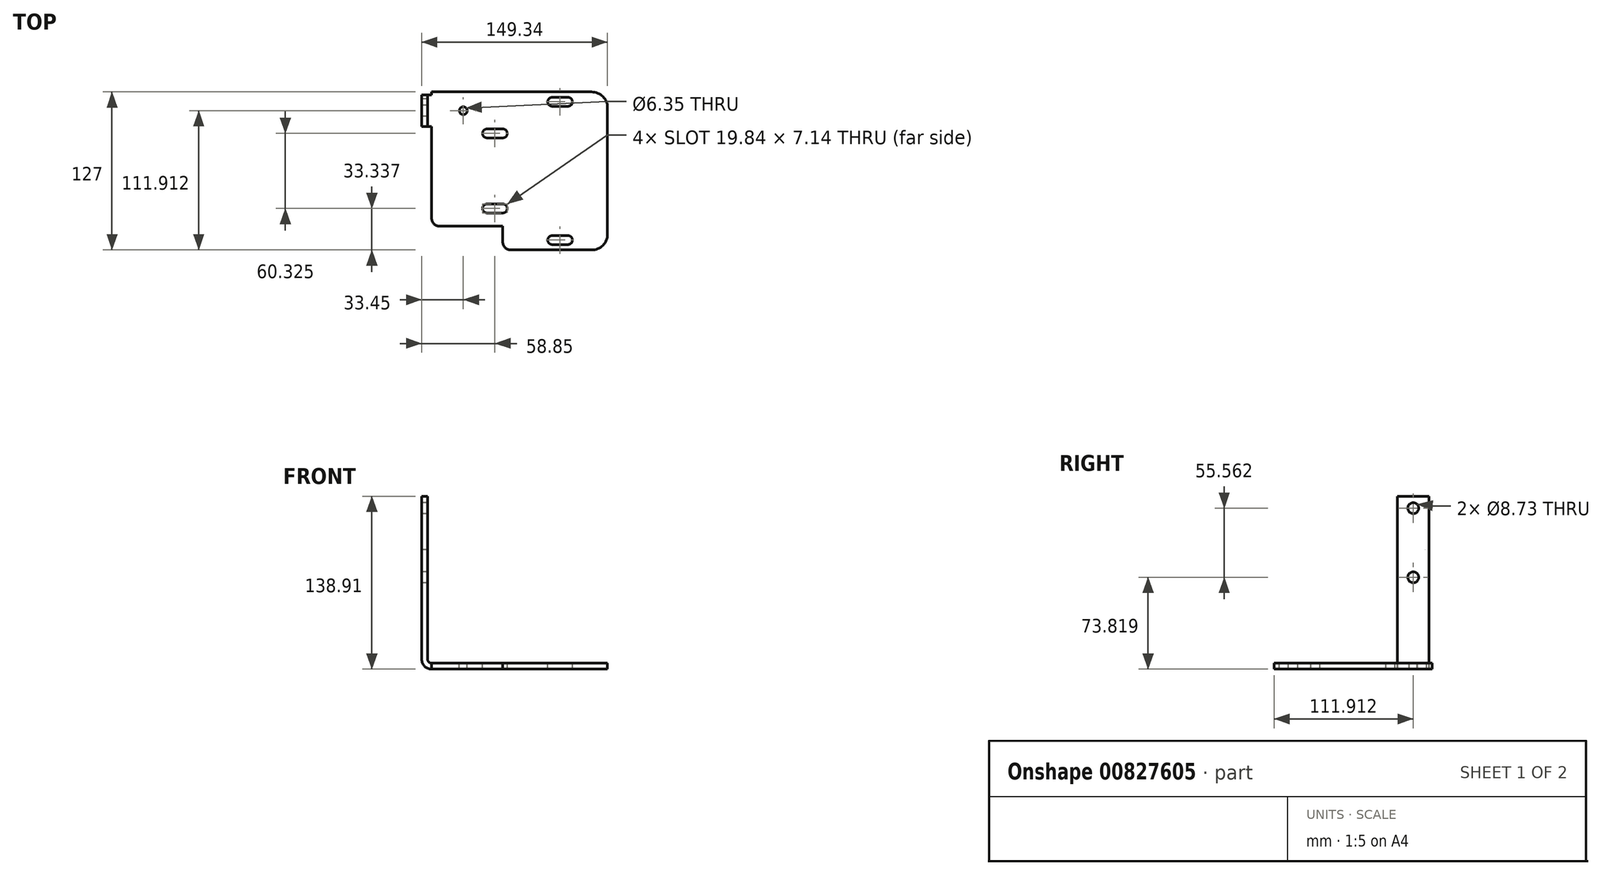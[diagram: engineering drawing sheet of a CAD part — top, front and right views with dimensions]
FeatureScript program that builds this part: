
annotation { "Feature Type Name" : "Feature", "Feature Type Description" : "" }
export const myFeature = defineFeature(function(context is Context, id is Id, definition is map)
    precondition{}
    {
        {
            var Q0;
            Q0=qCreatedBy(makeId("Front.planeOp"),FACE);
            var sketch = newSketch(context, id + "F0", { "sketchPlane" : qUnion([Q0])});
            skLineSegment(sketch, "E0", {"start": v(0, 0) * mm, "end": v(141.29, 0) * mm});
            skArc(sketch, "E1", {"start": v(-8.05, 8.05) * mm, "mid": v(-5.7, 2.36) * mm, "end": v(0, 0) * mm});
            skArc(sketch, "E2.0", {"start": v(-3.29, 8.05) * mm, "mid": v(-2.33, 5.73) * mm, "end": v(0, 4.76) * mm});
            skLineSegment(sketch, "E3", {"start": v(-8.05, 8.05) * mm, "end": v(-8.05, 138.9) * mm});
            skLineSegment(sketch, "E4", {"start": v(-8.05, 138.9) * mm, "end": v(-3.29, 138.9) * mm});
            skLineSegment(sketch, "E5", {"start": v(-3.29, 138.9) * mm, "end": v(-3.29, 8.05) * mm});
            skLineSegment(sketch, "E6", {"start": v(0, 4.76) * mm, "end": v(141.29, 4.76) * mm});
            skLineSegment(sketch, "E7", {"start": v(141.29, 0) * mm, "end": v(141.29, 4.76) * mm});
            skSolve(sketch);
        }
        {
            var Q0;
            Q0 = qSketchRegion(id + "F0", true);
            extrude(context, id + "F1", {"entities" : qUnion([Q0]), "oppositeDirection" : true, "depth" : 127 * mm, "offsetDistance" : 25.4 * mm});
        }
        {
            var Q0;
            Q0=makeQuery(id+"F1.opExtrude","SWEPT_FACE",FACE,{"disambiguationData":[OSD([sQuery(id+"F0.wireOp",EDGE,"E4")])]});
            var sketch = newSketch(context, id + "F2", { "sketchPlane" : qUnion([Q0])});
            skLineSegment(sketch, "E8.bottom", {"start": v(-8.05, 127) * mm, "end": v(0, 127) * mm});
            skLineSegment(sketch, "E8.top", {"start": v(-8.05, 124.61) * mm, "end": v(0, 124.61) * mm});
            skLineSegment(sketch, "E8.left", {"start": v(-8.05, 127) * mm, "end": v(-8.05, 124.61) * mm});
            skLineSegment(sketch, "E8.right", {"start": v(0, 127) * mm, "end": v(0, 124.61) * mm});
            skLineSegment(sketch, "E9.bottom", {"start": v(-8.05, 99.21) * mm, "end": v(0, 99.21) * mm});
            skLineSegment(sketch, "E9.top", {"start": v(-8.05, 0) * mm, "end": v(0, 0) * mm});
            skLineSegment(sketch, "E9.left", {"start": v(-8.05, 99.21) * mm, "end": v(-8.05, 0) * mm});
            skLineSegment(sketch, "E9.right", {"start": v(0, 99.21) * mm, "end": v(0, 0) * mm});
            skSolve(sketch);
        }
        {
            var Q0;
            Q0 = qSketchRegion(id + "F2", true);
            extrude(context, id + "F3", {"entities" : qUnion([Q0]), "operationType" : NewBodyOperationType.REMOVE, "endBound" : BoundingType.THROUGH_ALL, "oppositeDirection" : true, "depth" : 25.4 * mm, "offsetDistance" : 25.4 * mm});
        }
        {
            var Q0;
            Q0=makeQuery(id+"F1.opExtrude","SWEPT_FACE",FACE,{"disambiguationData":[OSD([sQuery(id+"F0.wireOp",EDGE,"E6")])]});
            var sketch = newSketch(context, id + "F4", { "sketchPlane" : qUnion([Q0])});
            skLineSegment(sketch, "E10.0", {"start": v(0, 127) * mm, "end": v(128.59, 127) * mm});
            skLineSegment(sketch, "E10.1", {"start": v(63.5, 0) * mm, "end": v(128.59, 0) * mm});
            skLineSegment(sketch, "E10.2", {"start": v(141.29, 114.3) * mm, "end": v(141.29, 12.7) * mm});
            skLineSegment(sketch, "E10.3", {"start": v(0, 25.4) * mm, "end": v(0, 99.21) * mm});
            skLineSegment(sketch, "E11", {"start": v(6.35, 19.05) * mm, "end": v(57.15, 19.05) * mm});
            skLineSegment(sketch, "E12", {"start": v(57.15, 19.05) * mm, "end": v(57.15, 6.35) * mm});
            skPoint(sketch, "E13.newPointA", {"position": v(57.15, 0) * mm});
            skPoint(sketch, "E13.newPointB", {"position": v(0, 0) * mm});
            skArc(sketch, "E13.filletArc", {"start": v(57.15, 6.35) * mm, "mid": v(59, 1.86) * mm, "end": v(63.5, 0) * mm});
            skPoint(sketch, "E14.newPointB", {"position": v(0, 19.05) * mm});
            skArc(sketch, "E14.filletArc", {"start": v(0, 25.4) * mm, "mid": v(1.86, 20.9) * mm, "end": v(6.35, 19.05) * mm});
            skPoint(sketch, "E15.visualSharp", {"position": v(141.29, 0) * mm});
            skPoint(sketch, "E16.visualSharp", {"position": v(141.29, 127) * mm});
            skArc(sketch, "E16.filletArc", {"start": v(141.29, 114.3) * mm, "mid": v(137.57, 123.28) * mm, "end": v(128.59, 127) * mm});
            skLineSegment(sketch, "E17", {"start": v(0, 99.21) * mm, "end": v(0, 127) * mm});
            skLineSegment(sketch, "E18", {"start": v(128.59, 127) * mm, "end": v(141.29, 127) * mm});
            skLineSegment(sketch, "E19", {"start": v(141.29, 127) * mm, "end": v(141.29, 114.3) * mm});
            skLineSegment(sketch, "E20", {"start": v(0, 0) * mm, "end": v(63.5, 0) * mm});
            skLineSegment(sketch, "E21", {"start": v(0, 0) * mm, "end": v(0, 25.4) * mm});
            skArc(sketch, "E22", {"start": v(57.15, 90.1) * mm, "mid": v(60.72, 93.66) * mm, "end": v(57.15, 97.23) * mm});
            skArc(sketch, "E23", {"start": v(44.45, 97.23) * mm, "mid": v(40.88, 93.66) * mm, "end": v(44.45, 90.1) * mm});
            skLineSegment(sketch, "E24", {"start": v(44.45, 97.23) * mm, "end": v(57.15, 97.23) * mm});
            skPoint(sketch, "E25", {"position": v(141.29, 63.5) * mm});
            skLineSegment(sketch, "E26", {"start": v(57.15, 90.1) * mm, "end": v(44.45, 90.1) * mm});
            skArc(sketch, "E27", {"start": v(57.03, 29.77) * mm, "mid": v(60.72, 33.28) * mm, "end": v(57.15, 36.9) * mm});
            skArc(sketch, "E28", {"start": v(44.45, 36.9) * mm, "mid": v(40.88, 33.34) * mm, "end": v(44.45, 29.77) * mm});
            skLineSegment(sketch, "E29", {"start": v(44.45, 36.9) * mm, "end": v(57.15, 36.9) * mm});
            skLineSegment(sketch, "E30", {"start": v(57.27, 29.77) * mm, "end": v(44.45, 29.77) * mm});
            skArc(sketch, "E31", {"start": v(109.52, 115.5) * mm, "mid": v(113.1, 119.06) * mm, "end": v(109.52, 122.63) * mm});
            skArc(sketch, "E32", {"start": v(96.82, 122.63) * mm, "mid": v(93.25, 119.05) * mm, "end": v(96.84, 115.5) * mm});
            skLineSegment(sketch, "E33", {"start": v(96.82, 122.63) * mm, "end": v(109.52, 122.63) * mm});
            skLineSegment(sketch, "E34.0", {"start": v(-8.05, 124.61) * mm, "end": v(-8.05, 99.21) * mm});
            skLineSegment(sketch, "E35", {"start": v(-8.05, 111.91) * mm, "end": v(25.4, 111.91) * mm});
            skCircle(sketch, "E36", {"center": v(25.4, 111.91) * mm, "radius": 3.18 * mm});
            skArc(sketch, "E37.filletArc", {"start": v(128.59, 0) * mm, "mid": v(137.57, 3.72) * mm, "end": v(141.29, 12.7) * mm});
            skArc(sketch, "E38", {"start": v(109.52, 4.37) * mm, "mid": v(113.1, 7.94) * mm, "end": v(109.52, 11.5) * mm});
            skArc(sketch, "E39", {"start": v(96.82, 11.5) * mm, "mid": v(93.25, 7.93) * mm, "end": v(96.84, 4.37) * mm});
            skLineSegment(sketch, "E40", {"start": v(96.82, 11.5) * mm, "end": v(109.52, 11.5) * mm});
            skLineSegment(sketch, "E41", {"start": v(109.52, 4.37) * mm, "end": v(96.84, 4.37) * mm});
            skLineSegment(sketch, "E42", {"start": v(109.52, 115.5) * mm, "end": v(96.84, 115.5) * mm});
            skSolve(sketch);
        }
        {
            var Q0;
            Q0=makeQuery(id+"F4.imprint","IMPRINT",FACE,{"disambiguationData":[TD([[makeQuery(id+"F4.imprint","IMPRINT",EDGE,{"derivedFrom":sQuery(id+"F4.wireOp",EDGE,"E22")}),1.0]])]});
            var Q1;
            {var subQ5=sQuery(id+"F4.wireOp",EDGE,"E32");Q1=makeQuery(id+"F4.imprint","IMPRINT",FACE,{"disambiguationData":[TD([[makeQuery(id+"F4.imprint","IMPRINT",EDGE,{"derivedFrom":subQ5}),1.0]])]});}
            var Q2;
            {var subQ5=sQuery(id+"F4.wireOp",EDGE,"E28");Q2=makeQuery(id+"F4.imprint","IMPRINT",FACE,{"disambiguationData":[TD([[makeQuery(id+"F4.imprint","IMPRINT",EDGE,{"derivedFrom":subQ5}),1.0]])]});}
            var Q3;
            Q3=makeQuery(id+"F4.imprint","IMPRINT",FACE,{"disambiguationData":[TD([[makeQuery(id+"F4.imprint","IMPRINT",EDGE,{"derivedFrom":sQuery(id+"F4.wireOp",EDGE,"4bc9b2f9-e6e9-4a17-9026-1413efbbbff0")}),1.0]])]});
            var Q4;
            Q4=makeQuery(id+"F4.imprint","IMPRINT",FACE,{"disambiguationData":[TD([[makeQuery(id+"F4.imprint","IMPRINT",EDGE,{"derivedFrom":sQuery(id+"F4.wireOp",EDGE,"E16.filletArc")}),-1.0]])]});
            var Q5;
            Q5=makeQuery(id+"F4.imprint","IMPRINT",FACE,{"disambiguationData":[TD([[makeQuery(id+"F4.imprint","IMPRINT",EDGE,{"derivedFrom":sQuery(id+"F4.wireOp",EDGE,"E15.filletArc")}),-1.0]])]});
            var Q6;
            Q6=makeQuery(id+"F4.imprint","IMPRINT",FACE,{"disambiguationData":[TD([[makeQuery(id+"F4.imprint","IMPRINT",EDGE,{"derivedFrom":sQuery(id+"F4.wireOp",EDGE,"E11")}),-1.0]])]});
            var Q7;
            Q7=makeQuery(id+"F4.imprint","IMPRINT",FACE,{"disambiguationData":[TD([[makeQuery(id+"F4.imprint","IMPRINT",EDGE,{"derivedFrom":sQuery(id+"F4.wireOp",EDGE,"E36")}),1.0]])]});
            var Q8;
            Q8=makeQuery(id+"F4.imprint","IMPRINT",FACE,{"disambiguationData":[TD([[makeQuery(id+"F4.imprint","IMPRINT",EDGE,{"derivedFrom":sQuery(id+"F4.wireOp",EDGE,"E38")}),1.0]])]});
            var Q9;
            {var subQ0=sQuery(id+"F4.wireOp",EDGE,"E37.filletArc");Q9=makeQuery(id+"F4.imprint","IMPRINT",FACE,{"disambiguationData":[TD([[makeQuery(id+"F4.imprint","IMPRINT",EDGE,{"derivedFrom":subQ0}),-1.0]])]});}
            extrude(context, id + "F5", {"entities" : qUnion([Q0, Q1, Q2, Q3, Q4, Q5, Q6, Q7, Q8, Q9]), "operationType" : NewBodyOperationType.REMOVE, "endBound" : BoundingType.THROUGH_ALL, "oppositeDirection" : true, "depth" : 25.4 * mm, "offsetDistance" : 25.4 * mm});
        }
        {
            var Q0;
            Q0=makeQuery(id+"F1.opExtrude","SWEPT_FACE",FACE,{"disambiguationData":[OSD([sQuery(id+"F0.wireOp",EDGE,"E3")])]});
            var sketch = newSketch(context, id + "F6", { "sketchPlane" : qUnion([Q0])});
            skLineSegment(sketch, "E43.0", {"start": v(-124.61, 138.9) * mm, "end": v(-99.21, 138.9) * mm});
            skLineSegment(sketch, "E43.1", {"start": v(-124.61, 8.05) * mm, "end": v(-124.61, 96.04) * mm});
            skLineSegment(sketch, "E43.2", {"start": v(-99.21, 8.05) * mm, "end": v(-99.21, 138.9) * mm});
            skCircle(sketch, "E44", {"center": v(-111.91, 129.38) * mm, "radius": 4.37 * mm});
            skPoint(sketch, "E44.centerSnap0", {"position": v(-111.91, 138.9) * mm});
            skCircle(sketch, "E45", {"center": v(-111.91, 73.82) * mm, "radius": 4.37 * mm});
            skArc(sketch, "E46", {"start": v(-121.5, 96.04) * mm, "mid": v(-116.67, 100.78) * mm, "end": v(-121.44, 105.57) * mm});
            skLineSegment(sketch, "E47", {"start": v(-121.38, 96.04) * mm, "end": v(-124.61, 96.04) * mm});
            skLineSegment(sketch, "E48", {"start": v(-121.44, 105.57) * mm, "end": v(-124.61, 105.57) * mm});
            skLineSegment(sketch, "E49.trimOffspring", {"start": v(-124.61, 105.57) * mm, "end": v(-124.61, 138.9) * mm});
            skLineSegment(sketch, "E50", {"start": v(-124.61, 105.57) * mm, "end": v(-124.61, 96.04) * mm});
            skSolve(sketch);
        }
        {
            var Q0;
            {var subQ3=sQuery(id+"F6.wireOp",EDGE,"E46");Q0=makeQuery(id+"F6.imprint","IMPRINT",FACE,{"disambiguationData":[TD([[makeQuery(id+"F6.imprint","IMPRINT",EDGE,{"derivedFrom":subQ3}),1.0]])]});}
            var Q1;
            Q1=makeQuery(id+"F6.imprint","IMPRINT",FACE,{"disambiguationData":[TD([[makeQuery(id+"F6.imprint","IMPRINT",EDGE,{"derivedFrom":sQuery(id+"F6.wireOp",EDGE,"E44")}),1.0]])]});
            var Q2;
            Q2=makeQuery(id+"F6.imprint","IMPRINT",FACE,{"disambiguationData":[TD([[makeQuery(id+"F6.imprint","IMPRINT",EDGE,{"derivedFrom":sQuery(id+"F6.wireOp",EDGE,"E45")}),1.0]])]});
            extrude(context, id + "F7", {"entities" : qUnion([Q0, Q1, Q2]), "operationType" : NewBodyOperationType.REMOVE, "endBound" : BoundingType.THROUGH_ALL, "oppositeDirection" : true, "depth" : 25.4 * mm, "offsetDistance" : 25.4 * mm});
        }
    });
